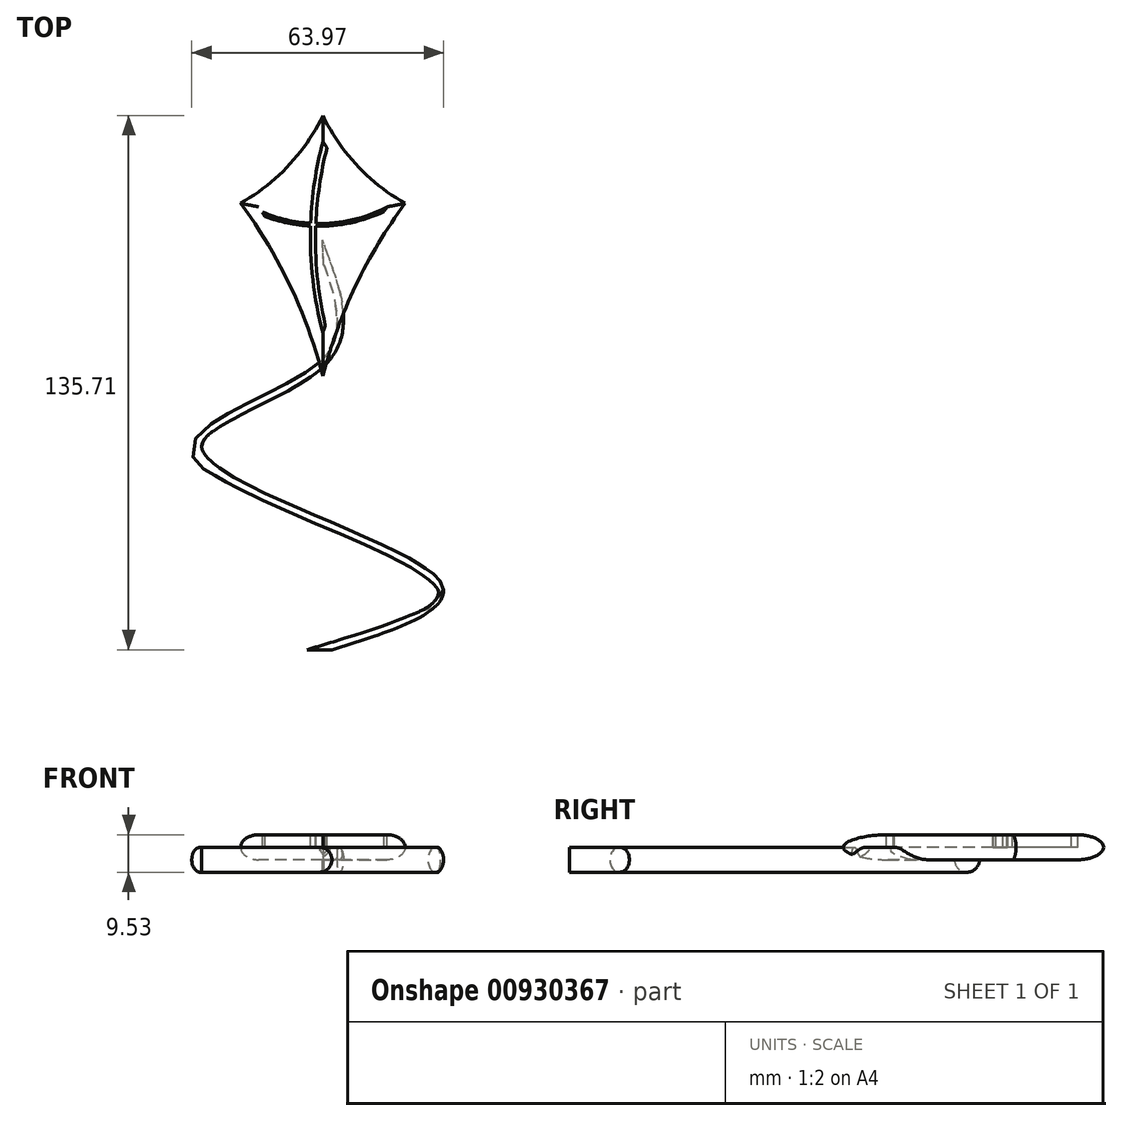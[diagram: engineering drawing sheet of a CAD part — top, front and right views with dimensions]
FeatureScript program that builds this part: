
annotation { "Feature Type Name" : "Feature", "Feature Type Description" : "" }
export const myFeature = defineFeature(function(context is Context, id is Id, definition is map)
    precondition{}
    {
        {
            var Q0;
            Q0=qCreatedBy(makeId("Top.planeOp"),FACE);
            var sketch = newSketch(context, id + "F0", { "sketchPlane" : qUnion([Q0])});
            skArc(sketch, "E0", {"start": v(-20.9, 11.58) * mm, "mid": v(-8.75, 21.1) * mm, "end": v(0, 33.84) * mm});
            skArc(sketch, "E1", {"start": v(0, -32.33) * mm, "mid": v(-8.33, -9.37) * mm, "end": v(-20.9, 11.58) * mm});
            skArc(sketch, "E2.MirrorCS", {"start": v(20.9, 11.58) * mm, "mid": v(8.75, 21.1) * mm, "end": v(0, 33.84) * mm});
            skArc(sketch, "E3.MirrorCS", {"start": v(0, -32.33) * mm, "mid": v(8.33, -9.37) * mm, "end": v(20.9, 11.58) * mm});
            skSolve(sketch);
        }
        {
            var Q0;
            Q0 = qSketchRegion(id + "F0", true);
            extrude(context, id + "F1", {"entities" : qUnion([Q0]), "depth" : 6.35 * mm, "offsetDistance" : 25.4 * mm});
        }
        {
            var Q0;
            Q0=makeQuery(id+"F1.opExtrude","CAP_EDGE",EDGE,{"disambiguationData":[OSD([sQuery(id+"F0.wireOp",EDGE,"E3.MirrorCS")])],"isStart":false});
            var Q1;
            Q1=makeQuery(id+"F1.opExtrude","CAP_EDGE",EDGE,{"disambiguationData":[OSD([sQuery(id+"F0.wireOp",EDGE,"E1")])],"isStart":false});
            var Q2;
            Q2=makeQuery(id+"F1.opExtrude","CAP_EDGE",EDGE,{"disambiguationData":[OSD([sQuery(id+"F0.wireOp",EDGE,"E0")])],"isStart":false});
            var Q3;
            Q3=makeQuery(id+"F1.opExtrude","CAP_EDGE",EDGE,{"disambiguationData":[OSD([sQuery(id+"F0.wireOp",EDGE,"E2.MirrorCS")])],"isStart":false});
            var Q4;
            Q4=makeQuery(id+"F1.opExtrude","CAP_EDGE",EDGE,{"disambiguationData":[OSD([sQuery(id+"F0.wireOp",EDGE,"E3.MirrorCS")])],"isStart":true});
            var Q5;
            Q5=makeQuery(id+"F1.opExtrude","CAP_EDGE",EDGE,{"disambiguationData":[OSD([sQuery(id+"F0.wireOp",EDGE,"E1")])],"isStart":true});
            var Q6;
            Q6=makeQuery(id+"F1.opExtrude","CAP_EDGE",EDGE,{"disambiguationData":[OSD([sQuery(id+"F0.wireOp",EDGE,"E0")])],"isStart":true});
            var Q7;
            Q7=makeQuery(id+"F1.opExtrude","CAP_EDGE",EDGE,{"disambiguationData":[OSD([sQuery(id+"F0.wireOp",EDGE,"E2.MirrorCS")])],"isStart":true});
            fillet(context, id + "F2", {"entities" : qUnion([Q0, Q1, Q2, Q3, Q4, Q5, Q6, Q7]), "radius" : 3.17 * mm, "tangentPropagation" : true, "allowEdgeOverflow" : false});
        }
        {
            var Q0;
            Q0=makeQuery(id+"F1.opExtrude","CAP_FACE",FACE,{"disambiguationData":[OSD([sQuery(id+"F0.wireOp",EDGE,"E0"),sQuery(id+"F0.wireOp",EDGE,"E1"),sQuery(id+"F0.wireOp",EDGE,"E2.MirrorCS"),sQuery(id+"F0.wireOp",EDGE,"E3.MirrorCS")])],"isStart":false});
            var sketch = newSketch(context, id + "F3", { "sketchPlane" : qUnion([Q0])});
            skArc(sketch, "E4", {"start": v(0, 27.28) * mm, "mid": v(-3.15, 2.97) * mm, "end": v(0, -21.34) * mm});
            skArc(sketch, "E5", {"start": v(1.05, 25.66) * mm, "mid": v(-1.86, 3.2) * mm, "end": v(0.61, -19.31) * mm});
            skLineSegment(sketch, "E6", {"start": v(0.61, -19.31) * mm, "end": v(0.61, -19.6) * mm});
            skSolve(sketch);
        }
        {
            var Q0;
            {var subQ2=sQuery(id+"F3.wireOp",EDGE,"E4");Q0=makeQuery(id+"F3.imprint","IMPRINT",FACE,{"disambiguationData":[TD([[makeQuery(id+"F3.imprint","IMPRINT",EDGE,{"derivedFrom":subQ2}),1.0]])]});}
            extrude(context, id + "F4", {"entities" : qUnion([Q0]), "operationType" : NewBodyOperationType.REMOVE, "oppositeDirection" : true, "depth" : 3.17 * mm, "offsetDistance" : 25.4 * mm});
        }
        {
            var Q0;
            {var subQ0=sQuery(id+"F3.wireOp",EDGE,"E5");var subQ1=sQuery(id+"F0.wireOp",EDGE,"E3.MirrorCS");var subQ3=sQuery(id+"F0.wireOp",EDGE,"E2.MirrorCS");var subQ5=sQuery(id+"F0.wireOp",EDGE,"E1");var subQ6=sQuery(id+"F0.wireOp",EDGE,"E0");var subQ7=makeQuery(id+"F1.opExtrude","CAP_FACE",FACE,{"disambiguationData":[OSD([subQ6,subQ5,subQ3,subQ1])],"isStart":false});Q0=makeQuery(id+"F4.boolean.opBoolean","SPLIT",FACE,{"disambiguationData":[TD([makeQuery(id+"F4.opExtrude","SWEPT_FACE",FACE,{"disambiguationData":[OSD([subQ0])]})])],"derivedFrom":subQ7});}
            var sketch = newSketch(context, id + "F5", { "sketchPlane" : qUnion([Q0])});
            skArc(sketch, "E7", {"start": v(-14.65, 8.18) * mm, "mid": v(0.57, 5.76) * mm, "end": v(15.52, 9.48) * mm});
            skArc(sketch, "E8", {"start": v(-15.28, 9.31) * mm, "mid": v(0.67, 6.46) * mm, "end": v(16.32, 10.65) * mm});
            skLineSegment(sketch, "E9", {"start": v(-15.28, 9.31) * mm, "end": v(-14.65, 8.18) * mm});
            skSolve(sketch);
        }
        {
            var Q0;
            {var subQ0=sQuery(id+"F5.wireOp",EDGE,"E7");var subQ6=makeQuery(id+"F4.boolean.opBoolean","COPY",EDGE,{"derivedFrom":makeQuery(id+"F4.opExtrude","CAP_EDGE",EDGE,{"disambiguationData":[OSD([sQuery(id+"F3.wireOp",EDGE,"E5")])],"isStart":true})});var subQ7=makeQuery(id+"F5.imprint","INTERSECT",VERTEX,{"derivedFrom":[subQ6,subQ0]});Q0=makeQuery(id+"F5.imprint","IMPRINT",FACE,{"disambiguationData":[TD([[makeQuery(id+"F5.imprint","IMPRINT",EDGE,{"disambiguationData":[TD([[subQ7,1.0]])],"derivedFrom":subQ6}),1.0]])]});}
            var Q1;
            {var subQ0=sQuery(id+"F5.wireOp",EDGE,"E9");Q1=makeQuery(id+"F5.imprint","IMPRINT",FACE,{"disambiguationData":[TD([[makeQuery(id+"F5.imprint","IMPRINT",EDGE,{"derivedFrom":subQ0}),1.0]])]});}
            extrude(context, id + "F6", {"entities" : qUnion([Q0, Q1]), "operationType" : NewBodyOperationType.REMOVE, "oppositeDirection" : true, "depth" : 3.17 * mm, "offsetDistance" : 25.4 * mm});
        }
        {
            var Q0;
            Q0=qCreatedBy(makeId("Front.planeOp"),FACE);
            cPlane(context, id + "F7", {"entities" : qUnion([Q0]), "cplaneType" : CPlaneType.OFFSET, "offset" : 101.6 * mm, "width" : 152.4 * mm, "height" : 152.4 * mm});
        }
        {
            var Q0;
            Q0=qCreatedBy(id+"F7.planeOp",FACE);
            var sketch = newSketch(context, id + "F8", { "sketchPlane" : qUnion([Q0])});
            skCircle(sketch, "E10", {"center": v(0, 0) * mm, "radius": 3.18 * mm});
            skSolve(sketch);
        }
        {
            var Q0;
            Q0=qCreatedBy(makeId("Top.planeOp"),FACE);
            var sketch = newSketch(context, id + "F9", { "sketchPlane" : qUnion([Q0])});
            skFitSpline(sketch, "E11", {"points": [v(0, 0) * mm, v(0, -28.99) * mm, v(-30.78, -51.43) * mm, v(28.72, -84.83) * mm, v(0, -101.87) * mm], "startDerivative": vector(55.13, -150) * mm, "endDerivative": vector(-221.35, -67.66) * mm});
            skSolve(sketch);
        }
        {
            var Q0;
            Q0=makeQuery(id+"F8.imprint","IMPRINT",FACE,{"disambiguationData":[TD([[makeQuery(id+"F8.imprint","IMPRINT",EDGE,{"derivedFrom":sQuery(id+"F8.wireOp",EDGE,"E10")}),1.0]])]});
            var Q1;
            Q1=sQuery(id+"F9.wireOp",EDGE,"E11");
            sweep(context, id + "F10", {"operationType" : NewBodyOperationType.ADD, "profiles" : qUnion([Q0]), "path" : qUnion([Q1])});
        }
    });
